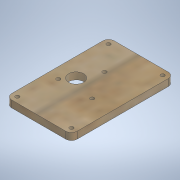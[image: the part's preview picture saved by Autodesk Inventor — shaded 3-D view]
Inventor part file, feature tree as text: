
AUTODESK INVENTOR PART (.ipt)
format: ipt  version: 2020.3 (Build 243373000, 373)  size: 162,816 bytes
history: native  units: mm
features: sketch x4, hole x3, other x1, extrude x1, fillet x1
ambient origin geometry x8: Origin, YZ Plane, XZ Plane, XY Plane, X Axis, Y Axis, Z Axis, Center Point
bodies: Body1 (feature_tree)
feature tree (10):
  other  "ソリッド1"
  extrude  "押し出し1"  Depth=81.509668mm
  hole  "穴1"  [1 undecoded]
  fillet  "フィレット1"  Radius=5.5mm
  hole  "穴2"  [1 undecoded]
  hole  "穴3"  [1 undecoded]
  sketch  "スケッチ1"
  sketch  "スケッチ2"
  sketch  "スケッチ3"
  sketch  "スケッチ4"
note: 3 required parameter values undecoded (feature->parameter linkage not recoverable at this tier; creation-order binding heuristic only, values carry confidence <= 0.55)
